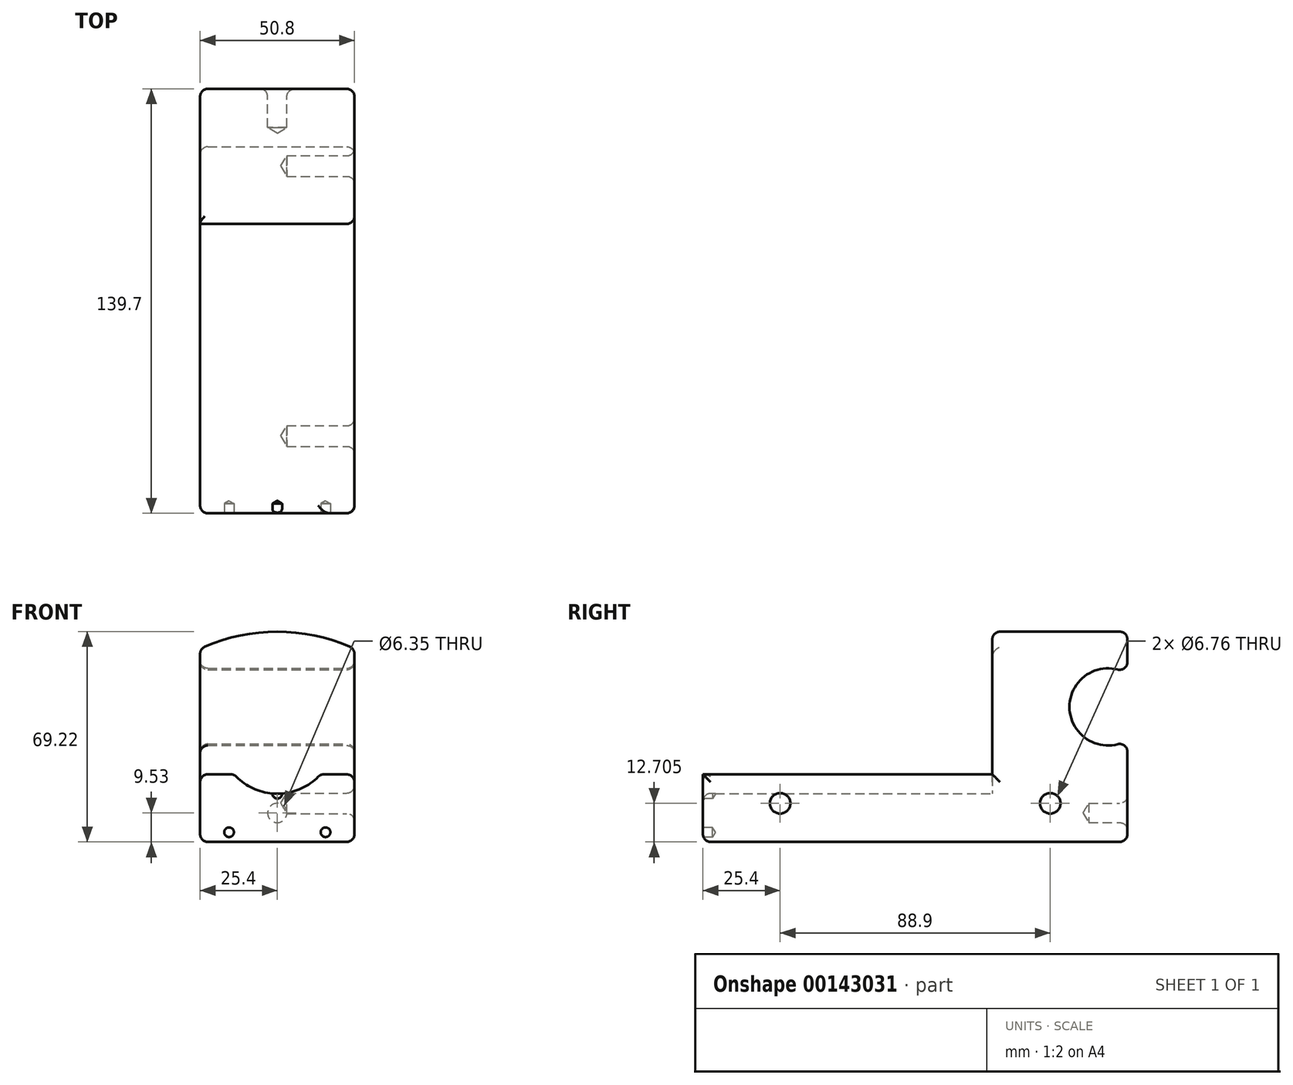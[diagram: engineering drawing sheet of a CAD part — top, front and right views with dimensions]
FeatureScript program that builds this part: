
annotation { "Feature Type Name" : "Feature", "Feature Type Description" : "" }
export const myFeature = defineFeature(function(context is Context, id is Id, definition is map)
    precondition{}
    {
        {
            var Q0;
            Q0=qCreatedBy(makeId("Front.planeOp"),FACE);
            var sketch = newSketch(context, id + "F0", { "sketchPlane" : qUnion([Q0])});
            skLineSegment(sketch, "E0.bottom", {"start": v(0, 0) * mm, "end": v(50.8, 0) * mm});
            skLineSegment(sketch, "E0.top", {"start": v(0, -22.23) * mm, "end": v(50.8, -22.23) * mm});
            skLineSegment(sketch, "E0.left", {"start": v(0, 0) * mm, "end": v(0, -22.23) * mm});
            skLineSegment(sketch, "E0.right", {"start": v(50.8, 0) * mm, "end": v(50.8, -22.23) * mm});
            skCircle(sketch, "E1", {"center": v(25.4, 12.7) * mm, "radius": 19.05 * mm});
            skPoint(sketch, "E1.centerSnap0", {"position": v(25.4, 0) * mm});
            skSolve(sketch);
        }
        {
            var Q0;
            {var subQ0=sQuery(id+"F0.wireOp",EDGE,"E1");var subQ1=sQuery(id+"F0.wireOp",EDGE,"E0.bottom");var subQ2=makeQuery(id+"F0.imprint","INTERSECT",VERTEX,{"disambiguationData":[OD(0.0)],"derivedFrom":[subQ1,subQ0]});Q0=makeQuery(id+"F0.imprint","IMPRINT",FACE,{"disambiguationData":[TD([[makeQuery(id+"F0.imprint","IMPRINT",EDGE,{"disambiguationData":[TD([[subQ2,-1.0]])],"derivedFrom":subQ1}),1.0]])]});}
            var Q1;
            {var subQ0=sQuery(id+"F0.wireOp",EDGE,"E1");var subQ1=sQuery(id+"F0.wireOp",EDGE,"E0.bottom");var subQ2=makeQuery(id+"F0.imprint","INTERSECT",VERTEX,{"disambiguationData":[OD(0.0)],"derivedFrom":[subQ1,subQ0]});Q1=makeQuery(id+"F0.imprint","IMPRINT",FACE,{"disambiguationData":[TD([[makeQuery(id+"F0.imprint","IMPRINT",EDGE,{"disambiguationData":[TD([[subQ2,-1.0]])],"derivedFrom":subQ1}),-1.0]])]});}
            var Q2;
            Q2=makeQuery(id+"F0.imprint","IMPRINT",FACE,{"disambiguationData":[TD([[makeQuery(id+"F0.imprint","IMPRINT",EDGE,{"derivedFrom":sQuery(id+"F0.wireOp",EDGE,"E0.top")}),1.0]])]});
            extrude(context, id + "F1", {"entities" : qUnion([Q0, Q1, Q2]), "depth" : 95.25 * mm});
        }
        {
            var Q0;
            Q0=makeQuery(id+"F1.opExtrude","CAP_FACE",FACE,{"disambiguationData":[OSD([sQuery(id+"F0.wireOp",EDGE,"E0.bottom"),sQuery(id+"F0.wireOp",EDGE,"E0.top"),sQuery(id+"F0.wireOp",EDGE,"E0.left"),sQuery(id+"F0.wireOp",EDGE,"E0.right"),sQuery(id+"F0.wireOp",EDGE,"E1")])],"isStart":true});
            var sketch = newSketch(context, id + "F2", { "sketchPlane" : qUnion([Q0])});
            skArc(sketch, "E2", {"start": v(0, 41.32) * mm, "mid": v(-25.4, 47) * mm, "end": v(-50.8, 41.32) * mm});
            skPoint(sketch, "E2.centerSnap0", {"position": v(-25.4, 31.75) * mm});
            skLineSegment(sketch, "E3", {"start": v(-50.8, -22.23) * mm, "end": v(-50.8, 41.32) * mm});
            skLineSegment(sketch, "E4", {"start": v(0, -22.23) * mm, "end": v(0, 41.32) * mm});
            skLineSegment(sketch, "E5", {"start": v(-50.8, -22.23) * mm, "end": v(0, -22.23) * mm});
            skSolve(sketch);
        }
        {
            var Q0;
            {var subQ4=sQuery(id+"F2.wireOp",EDGE,"E2");Q0=makeQuery(id+"F2.imprint","IMPRINT",FACE,{"disambiguationData":[TD([[makeQuery(id+"F2.imprint","IMPRINT",EDGE,{"derivedFrom":subQ4}),1.0]])]});}
            var Q1;
            {var subQ3=sQuery(id+"F2.wireOp",EDGE,"E5");Q1=makeQuery(id+"F2.imprint","IMPRINT",FACE,{"disambiguationData":[TD([[makeQuery(id+"F2.imprint","IMPRINT",EDGE,{"derivedFrom":subQ3}),-1.0]])]});}
            extrude(context, id + "F3", {"entities" : qUnion([Q0, Q1]), "operationType" : NewBodyOperationType.ADD, "depth" : 44.45 * mm});
        }
        {
            var Q0;
            Q0=makeQuery(id+"F3.opExtrude","CAP_FACE",FACE,{"disambiguationData":[OSD([sQuery(id+"F2.wireOp",EDGE,"E2"),sQuery(id+"F2.wireOp",EDGE,"E3"),sQuery(id+"F2.wireOp",EDGE,"E4"),sQuery(id+"F2.wireOp",EDGE,"E5")])],"isStart":false});
            var sketch = newSketch(context, id + "F4", { "sketchPlane" : qUnion([Q0])});
            skCircle(sketch, "E6", {"center": v(-25.4, -12.7) * mm, "radius": 3.18 * mm});
            skSolve(sketch);
        }
        {
            var Q0;
            Q0=sQuery(id+"F4.wireOp",VERTEX,"E6.center");
            var Q1;
            Q1=makeQuery(id+"F1.opExtrude","SWEPT_BODY",BODY,{"disambiguationData":[OSD([sQuery(id+"F0.wireOp",EDGE,"E0.bottom"),sQuery(id+"F0.wireOp",EDGE,"E0.top"),sQuery(id+"F0.wireOp",EDGE,"E0.left"),sQuery(id+"F0.wireOp",EDGE,"E0.right"),sQuery(id+"F0.wireOp",EDGE,"E1")])]});
            hole(context, id + "F5", {"style" : HoleStyle.SIMPLE, "endStyle" : HoleEndStyle.BLIND, "holeDiameter" : 6.35 * mm, "holeDepth" : 12.7 * mm, "locations" : qUnion([Q0]), "scope" : qUnion([Q1])});
        }
        {
            var Q0;
            Q0=makeQuery(id+"F3.boolean.opBoolean","MERGE",FACE,{"derivedFrom":[makeQuery(id+"F1.opExtrude","SWEPT_FACE",FACE,{"disambiguationData":[OSD([sQuery(id+"F0.wireOp",EDGE,"E0.right")])]}),makeQuery(id+"F3.opExtrude","SWEPT_FACE",FACE,{"disambiguationData":[OSD([sQuery(id+"F2.wireOp",EDGE,"E3")])]})]});
            var sketch = newSketch(context, id + "F6", { "sketchPlane" : qUnion([Q0])});
            skCircle(sketch, "E7", {"center": v(19.05, -9.53) * mm, "radius": 3.18 * mm});
            skCircle(sketch, "E8", {"center": v(-69.85, -9.53) * mm, "radius": 3.18 * mm});
            skSolve(sketch);
        }
        {
            var Q0;
            Q0=sQuery(id+"F6.wireOp",VERTEX,"E7.center");
            var Q1;
            Q1=sQuery(id+"F6.wireOp",VERTEX,"E8.center");
            var Q2;
            Q2=makeQuery(id+"F1.opExtrude","SWEPT_BODY",BODY,{"disambiguationData":[OSD([sQuery(id+"F0.wireOp",EDGE,"E0.bottom"),sQuery(id+"F0.wireOp",EDGE,"E0.top"),sQuery(id+"F0.wireOp",EDGE,"E0.left"),sQuery(id+"F0.wireOp",EDGE,"E0.right"),sQuery(id+"F0.wireOp",EDGE,"E1")])]});
            hole(context, id + "F7", {"style" : HoleStyle.SIMPLE, "endStyle" : HoleEndStyle.BLIND, "standardTappedOrClearance" : lookupTablePath({ "standard" : "ANSI", "fit" : "Normal (ASME)", "size" : "1/4", "type" : "Clearance" }), "standardBlindInLast" : lookupTablePath({ "fit" : "Free", "standard" : "ANSI", "size" : "1/4", "type" : "Clearance" }), "holeDiameter" : 6.76 * mm, "holeDepth" : 22.22 * mm, "startFromSketch" : true, "locations" : qUnion([Q0, Q1]), "scope" : qUnion([Q2])});
        }
        {
            var Q0;
            Q0=makeQuery(id+"F3.boolean.opBoolean","MERGE",FACE,{"derivedFrom":[makeQuery(id+"F1.opExtrude","SWEPT_FACE",FACE,{"disambiguationData":[OSD([sQuery(id+"F0.wireOp",EDGE,"E0.right")])]}),makeQuery(id+"F3.opExtrude","SWEPT_FACE",FACE,{"disambiguationData":[OSD([sQuery(id+"F2.wireOp",EDGE,"E3")])]})]});
            var Q1;
            Q1=makeQuery(id+"F3.boolean.opBoolean","MERGE",FACE,{"derivedFrom":[makeQuery(id+"F1.opExtrude","SWEPT_FACE",FACE,{"disambiguationData":[OSD([sQuery(id+"F0.wireOp",EDGE,"E0.left")])]}),makeQuery(id+"F3.opExtrude","SWEPT_FACE",FACE,{"disambiguationData":[OSD([sQuery(id+"F2.wireOp",EDGE,"E4")])]})]});
            cPlane(context, id + "F8", {"entities" : qUnion([Q0, Q1]), "cplaneType" : CPlaneType.MID_PLANE, "offset" : 25.4 * mm, "width" : 152.4 * mm, "height" : 152.4 * mm});
        }
        {
            var Q0;
            Q0=makeQuery(id+"F3.boolean.opBoolean","MERGE",FACE,{"derivedFrom":[makeQuery(id+"F1.opExtrude","SWEPT_FACE",FACE,{"disambiguationData":[OSD([sQuery(id+"F0.wireOp",EDGE,"E0.right")])]}),makeQuery(id+"F3.opExtrude","SWEPT_FACE",FACE,{"disambiguationData":[OSD([sQuery(id+"F2.wireOp",EDGE,"E3")])]})]});
            var sketch = newSketch(context, id + "F9", { "sketchPlane" : qUnion([Q0])});
            skCircle(sketch, "E9", {"center": v(38.1, 22.22) * mm, "radius": 12.7 * mm});
            skSolve(sketch);
        }
        {
            var Q0;
            {var subQ0=sQuery(id+"F9.wireOp",EDGE,"E9");var subQ1=makeQuery(id+"F3.opExtrude","CAP_EDGE",EDGE,{"disambiguationData":[OSD([sQuery(id+"F2.wireOp",EDGE,"E3")])],"isStart":false});var subQ2=makeQuery(id+"F9.imprint","INTERSECT",VERTEX,{"disambiguationData":[OD(0.0)],"derivedFrom":[subQ1,subQ0]});Q0=makeQuery(id+"F9.imprint","IMPRINT",FACE,{"disambiguationData":[TD([[makeQuery(id+"F9.imprint","IMPRINT",EDGE,{"disambiguationData":[TD([[subQ2,1.0]])],"derivedFrom":subQ0}),1.0]])]});}
            var Q1;
            {var subQ0=sQuery(id+"F9.wireOp",EDGE,"E9");var subQ1=makeQuery(id+"F3.opExtrude","CAP_EDGE",EDGE,{"disambiguationData":[OSD([sQuery(id+"F2.wireOp",EDGE,"E3")])],"isStart":false});var subQ2=makeQuery(id+"F9.imprint","INTERSECT",VERTEX,{"disambiguationData":[OD(0.0)],"derivedFrom":[subQ1,subQ0]});Q1=makeQuery(id+"F9.imprint","IMPRINT",FACE,{"disambiguationData":[TD([[makeQuery(id+"F9.imprint","IMPRINT",EDGE,{"disambiguationData":[TD([[subQ2,-1.0]])],"derivedFrom":subQ0}),1.0]])]});}
            extrude(context, id + "F10", {"entities" : qUnion([Q0, Q1]), "operationType" : NewBodyOperationType.REMOVE, "endBound" : BoundingType.THROUGH_ALL, "oppositeDirection" : true, "depth" : 25.4 * mm});
        }
        {
            var Q0;
            Q0=makeQuery(id+"F1.opExtrude","CAP_FACE",FACE,{"disambiguationData":[OSD([sQuery(id+"F0.wireOp",EDGE,"E0.bottom"),sQuery(id+"F0.wireOp",EDGE,"E0.top"),sQuery(id+"F0.wireOp",EDGE,"E0.left"),sQuery(id+"F0.wireOp",EDGE,"E0.right"),sQuery(id+"F0.wireOp",EDGE,"E1")])],"isStart":false});
            var sketch = newSketch(context, id + "F11", { "sketchPlane" : qUnion([Q0])});
            skCircle(sketch, "E10", {"center": v(9.53, -19.05) * mm, "radius": 1.59 * mm});
            skCircle(sketch, "E11", {"center": v(41.28, -19.05) * mm, "radius": 1.59 * mm});
            skCircle(sketch, "E12", {"center": v(25.4, -6.35) * mm, "radius": 1.59 * mm});
            skSolve(sketch);
        }
        {
            var Q0;
            Q0=sQuery(id+"F11.wireOp",VERTEX,"E12.center");
            var Q1;
            Q1=sQuery(id+"F11.wireOp",VERTEX,"E11.center");
            var Q2;
            Q2=sQuery(id+"F11.wireOp",VERTEX,"E10.center");
            var Q3;
            Q3=makeQuery(id+"F1.opExtrude","SWEPT_BODY",BODY,{"disambiguationData":[OSD([sQuery(id+"F0.wireOp",EDGE,"E0.bottom"),sQuery(id+"F0.wireOp",EDGE,"E0.top"),sQuery(id+"F0.wireOp",EDGE,"E0.left"),sQuery(id+"F0.wireOp",EDGE,"E0.right"),sQuery(id+"F0.wireOp",EDGE,"E1")])]});
            hole(context, id + "F12", {"style" : HoleStyle.SIMPLE, "endStyle" : HoleEndStyle.BLIND, "holeDiameter" : 3.17 * mm, "holeDepth" : 3.17 * mm, "startFromSketch" : true, "locations" : qUnion([Q0, Q1, Q2]), "scope" : qUnion([Q3])});
        }
        {
            var Q0;
            {var subQ0=sQuery(id+"F0.wireOp",EDGE,"E0.bottom");Q0=makeQuery(id+"F1.opExtrude","SWEPT_FACE",FACE,{"disambiguationData":[OSD([subQ0]),TDD([makeQuery(id+"F0.imprint","IMPRINT",EDGE,{"disambiguationData":[TD([[makeQuery(id+"F0.imprint","INTERSECT",VERTEX,{"derivedFrom":[subQ0,sQuery(id+"F0.wireOp",EDGE,"E0.right")]}),1.0]])],"derivedFrom":subQ0})])]});}
            cPlane(context, id + "F13", {"entities" : qUnion([Q0]), "cplaneType" : CPlaneType.OFFSET, "offset" : 41.27 * mm, "width" : 152.4 * mm, "height" : 152.4 * mm});
        }
        {
            var Q0;
            Q0=qCreatedBy(id+"F13.planeOp",FACE);
            var sketch = newSketch(context, id + "F14", { "sketchPlane" : qUnion([Q0])});
            skLineSegment(sketch, "E13", {"start": v(44.45, 0) * mm, "end": v(44.45, -95.25) * mm});
            skLineSegment(sketch, "E14", {"start": v(6.35, -95.25) * mm, "end": v(6.35, 0) * mm});
            skCircle(sketch, "E15", {"center": v(25.4, -73.03) * mm, "radius": 6.35 * mm});
            skSolve(sketch);
        }
        {
            var Q0;
            Q0=makeQuery(id+"F14.imprint","IMPRINT",FACE,{"disambiguationData":[TD([[makeQuery(id+"F14.imprint","IMPRINT",EDGE,{"derivedFrom":sQuery(id+"F14.wireOp",EDGE,"E15")}),1.0]])]});
            extrude(context, id + "F15", {"entities" : qUnion([Q0]), "operationType" : NewBodyOperationType.REMOVE, "oppositeDirection" : true, "depth" : 12.7 * mm});
        }
        {
            var Q0;
            {var subQ0=sQuery(id+"F0.wireOp",EDGE,"E1");var subQ1=sQuery(id+"F0.wireOp",EDGE,"E0.bottom");Q0=makeQuery(id+"F1.opExtrude","SWEPT_EDGE",EDGE,{"disambiguationData":[OSD([subQ1,subQ0]),TDD([makeQuery(id+"F0.imprint","INTERSECT",VERTEX,{"disambiguationData":[OD(1.0)],"derivedFrom":[subQ1,subQ0]})])]});}
            var Q1;
            Q1=makeQuery(id+"F3.boolean.opBoolean","MERGE",FACE,{"derivedFrom":[makeQuery(id+"F1.opExtrude","SWEPT_FACE",FACE,{"disambiguationData":[OSD([sQuery(id+"F0.wireOp",EDGE,"E0.right")])]}),makeQuery(id+"F3.opExtrude","SWEPT_FACE",FACE,{"disambiguationData":[OSD([sQuery(id+"F2.wireOp",EDGE,"E3")])]})]});
            var Q2;
            Q2=makeQuery(id+"F3.opExtrude","CAP_EDGE",EDGE,{"disambiguationData":[OSD([sQuery(id+"F2.wireOp",EDGE,"E3")])],"isStart":true});
            var Q3;
            Q3=makeQuery(id+"F1.opExtrude","CAP_EDGE",EDGE,{"disambiguationData":[OSD([sQuery(id+"F0.wireOp",EDGE,"E1")])],"isStart":true});
            var Q4;
            {var subQ0=sQuery(id+"F0.wireOp",EDGE,"E0.bottom");Q4=makeQuery(id+"F1.opExtrude","CAP_EDGE",EDGE,{"disambiguationData":[OSD([subQ0]),TDD([makeQuery(id+"F0.imprint","IMPRINT",EDGE,{"disambiguationData":[TD([[makeQuery(id+"F0.imprint","INTERSECT",VERTEX,{"derivedFrom":[subQ0,sQuery(id+"F0.wireOp",EDGE,"E0.right")]}),1.0]])],"derivedFrom":subQ0})])],"isStart":true});}
            var Q5;
            Q5=makeQuery(id+"F3.opExtrude","CAP_EDGE",EDGE,{"disambiguationData":[OSD([sQuery(id+"F2.wireOp",EDGE,"E2")])],"isStart":true});
            var Q6;
            Q6=makeQuery(id+"F1.opExtrude","CAP_EDGE",EDGE,{"disambiguationData":[OSD([sQuery(id+"F0.wireOp",EDGE,"E1")])],"isStart":false});
            var Q7;
            {var subQ0=sQuery(id+"F0.wireOp",EDGE,"E0.bottom");Q7=makeQuery(id+"F1.opExtrude","CAP_EDGE",EDGE,{"disambiguationData":[OSD([subQ0]),TDD([makeQuery(id+"F0.imprint","IMPRINT",EDGE,{"disambiguationData":[TD([[makeQuery(id+"F0.imprint","INTERSECT",VERTEX,{"derivedFrom":[subQ0,sQuery(id+"F0.wireOp",EDGE,"E0.left")]}),-1.0]])],"derivedFrom":subQ0})])],"isStart":false});}
            var Q8;
            Q8=makeQuery(id+"F1.opExtrude","CAP_EDGE",EDGE,{"disambiguationData":[OSD([sQuery(id+"F0.wireOp",EDGE,"E0.left")])],"isStart":false});
            var Q9;
            Q9=makeQuery(id+"F1.opExtrude","CAP_EDGE",EDGE,{"disambiguationData":[OSD([sQuery(id+"F0.wireOp",EDGE,"E0.top")])],"isStart":false});
            var Q10;
            {var subQ0=sQuery(id+"F0.wireOp",EDGE,"E1");var subQ1=sQuery(id+"F0.wireOp",EDGE,"E0.bottom");Q10=makeQuery(id+"F1.opExtrude","SWEPT_EDGE",EDGE,{"disambiguationData":[OSD([subQ1,subQ0]),TDD([makeQuery(id+"F0.imprint","INTERSECT",VERTEX,{"disambiguationData":[OD(0.0)],"derivedFrom":[subQ1,subQ0]})])]});}
            var Q11;
            Q11=makeQuery(id+"F1.opExtrude","SWEPT_EDGE",EDGE,{"disambiguationData":[OSD([sQuery(id+"F0.wireOp",EDGE,"E0.bottom"),sQuery(id+"F0.wireOp",EDGE,"E0.left")])]});
            var Q12;
            {var subQ0=sQuery(id+"F0.wireOp",EDGE,"E0.bottom");Q12=makeQuery(id+"F1.opExtrude","CAP_EDGE",EDGE,{"disambiguationData":[OSD([subQ0]),TDD([makeQuery(id+"F0.imprint","IMPRINT",EDGE,{"disambiguationData":[TD([[makeQuery(id+"F0.imprint","INTERSECT",VERTEX,{"derivedFrom":[subQ0,sQuery(id+"F0.wireOp",EDGE,"E0.left")]}),-1.0]])],"derivedFrom":subQ0})])],"isStart":true});}
            var Q13;
            Q13=makeQuery(id+"F3.opExtrude","SWEPT_EDGE",EDGE,{"disambiguationData":[OSD([sQuery(id+"F2.wireOp",EDGE,"E2"),sQuery(id+"F2.wireOp",EDGE,"E4")])]});
            var Q14;
            Q14=makeQuery(id+"F10.boolean.opBoolean","INTERSECT",EDGE,{"derivedFrom":[makeQuery(id+"F3.boolean.opBoolean","MERGE",FACE,{"derivedFrom":[makeQuery(id+"F1.opExtrude","SWEPT_FACE",FACE,{"disambiguationData":[OSD([sQuery(id+"F0.wireOp",EDGE,"E0.left")])]}),makeQuery(id+"F3.opExtrude","SWEPT_FACE",FACE,{"disambiguationData":[OSD([sQuery(id+"F2.wireOp",EDGE,"E4")])]})]}),makeQuery(id+"F10.opExtrude","SWEPT_FACE",FACE,{"disambiguationData":[OSD([sQuery(id+"F9.wireOp",EDGE,"E9")])]})]});
            var Q15;
            {var subQ0=sQuery(id+"F2.wireOp",EDGE,"E4");var subQ1=sQuery(id+"F2.wireOp",EDGE,"E2");Q15=makeQuery(id+"F10.boolean.opBoolean","SPLIT",EDGE,{"disambiguationData":[TD([makeQuery(id+"F3.opExtrude","SWEPT_FACE",FACE,{"disambiguationData":[OSD([subQ1])]})])],"derivedFrom":makeQuery(id+"F3.opExtrude","CAP_EDGE",EDGE,{"disambiguationData":[OSD([subQ0])],"isStart":false})});}
            var Q16;
            {var subQ1=sQuery(id+"F2.wireOp",EDGE,"E4");Q16=makeQuery(id+"F10.boolean.opBoolean","SPLIT",EDGE,{"disambiguationData":[TD([makeQuery(id+"F1.opExtrude","SWEPT_FACE",FACE,{"disambiguationData":[OSD([sQuery(id+"F0.wireOp",EDGE,"E0.top")])]})])],"derivedFrom":makeQuery(id+"F3.opExtrude","CAP_EDGE",EDGE,{"disambiguationData":[OSD([subQ1])],"isStart":false})});}
            var Q17;
            Q17=makeQuery(id+"F3.boolean.opBoolean","MERGE",EDGE,{"derivedFrom":[makeQuery(id+"F1.opExtrude","SWEPT_EDGE",EDGE,{"disambiguationData":[OSD([sQuery(id+"F0.wireOp",EDGE,"E0.top"),sQuery(id+"F0.wireOp",EDGE,"E0.left")])]}),makeQuery(id+"F3.opExtrude","SWEPT_EDGE",EDGE,{"disambiguationData":[OSD([sQuery(id+"F2.wireOp",EDGE,"E4"),sQuery(id+"F2.wireOp",EDGE,"E5")])]})]});
            var Q18;
            Q18=makeQuery(id+"F3.opExtrude","CAP_EDGE",EDGE,{"disambiguationData":[OSD([sQuery(id+"F2.wireOp",EDGE,"E2")])],"isStart":false});
            var Q19;
            Q19=makeQuery(id+"F10.boolean.opBoolean","INTERSECT",EDGE,{"disambiguationData":[OD(0.0)],"derivedFrom":[makeQuery(id+"F3.opExtrude","CAP_FACE",FACE,{"disambiguationData":[OSD([sQuery(id+"F2.wireOp",EDGE,"E2"),sQuery(id+"F2.wireOp",EDGE,"E3"),sQuery(id+"F2.wireOp",EDGE,"E4"),sQuery(id+"F2.wireOp",EDGE,"E5")])],"isStart":false}),makeQuery(id+"F10.opExtrude","SWEPT_FACE",FACE,{"disambiguationData":[OSD([sQuery(id+"F9.wireOp",EDGE,"E9")])]})]});
            var Q20;
            {var subQ0=sQuery(id+"F2.wireOp",EDGE,"E3");var subQ1=sQuery(id+"F2.wireOp",EDGE,"E4");var subQ2=sQuery(id+"F2.wireOp",EDGE,"E5");Q20=makeQuery(id+"F10.boolean.opBoolean","SPLIT",FACE,{"disambiguationData":[TD([makeQuery(id+"F1.opExtrude","SWEPT_FACE",FACE,{"disambiguationData":[OSD([sQuery(id+"F0.wireOp",EDGE,"E0.top")])]})])],"derivedFrom":makeQuery(id+"F3.opExtrude","CAP_FACE",FACE,{"disambiguationData":[OSD([sQuery(id+"F2.wireOp",EDGE,"E2"),subQ0,subQ1,subQ2])],"isStart":false})});}
            fillet(context, id + "F16", {"entities" : qUnion([Q0, Q1, Q2, Q3, Q4, Q5, Q6, Q7, Q8, Q9, Q10, Q11, Q12, Q13, Q14, Q15, Q16, Q17, Q18, Q19, Q20]), "radius" : 2.54 * mm, "tangentPropagation" : true, "allowEdgeOverflow" : false});
        }
    });
